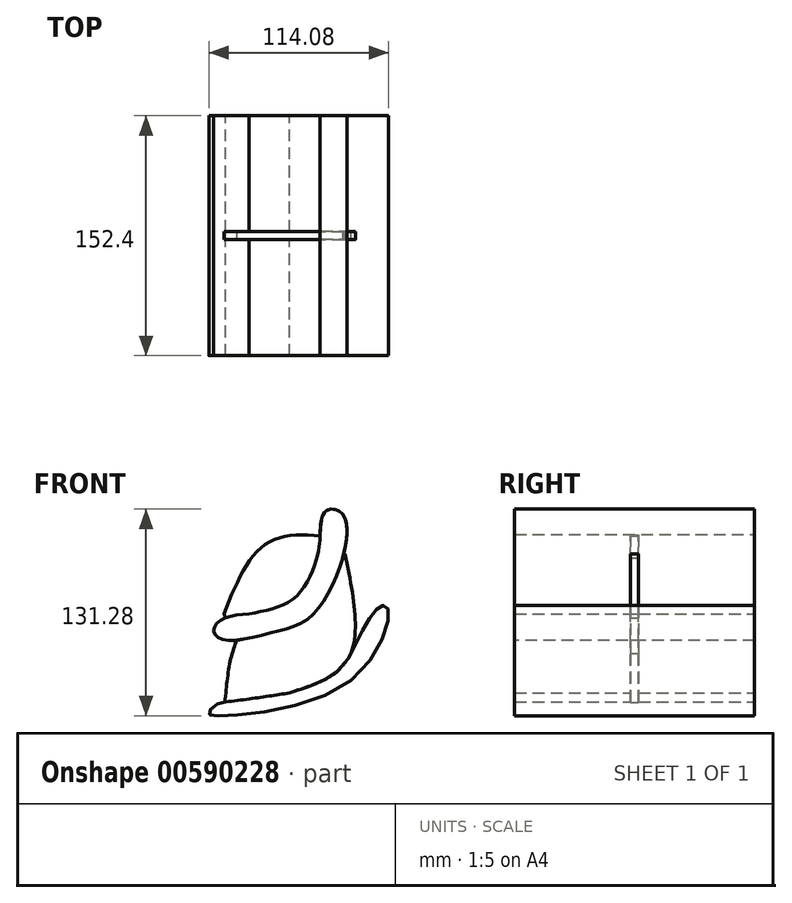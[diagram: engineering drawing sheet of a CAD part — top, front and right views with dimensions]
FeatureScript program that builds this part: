
annotation { "Feature Type Name" : "Feature", "Feature Type Description" : "" }
export const myFeature = defineFeature(function(context is Context, id is Id, definition is map)
    precondition{}
    {
        {
            var Q0;
            Q0=qCreatedBy(makeId("Front.planeOp"),FACE);
            var sketch = newSketch(context, id + "F0", { "sketchPlane" : qUnion([Q0])});
            skLineSegment(sketch, "E0.bottom", {"start": v(0, 0) * mm, "end": v(-60.89, 0) * mm});
            skFitSpline(sketch, "E1", {"points": [v(-60.89, 0) * mm, v(-30.65, 11.3) * mm, v(-16.9, 39.17) * mm, v(-15.76, 50.24) * mm], "startDerivative": vector(86.43, 14.9) * mm, "endDerivative": vector(0.82, 41.24) * mm});
            skFitSpline(sketch, "E2", {"points": [v(-60.89, 0) * mm, v(-77.99, -3.6) * mm, v(-83.33, -10.85) * mm, v(-77.22, -16.57) * mm, v(-44.77, -11.6) * mm, v(-16.9, 3.28) * mm, v(0, 60.93) * mm, v(-11.56, 65.51) * mm, v(-15.76, 50.24) * mm], "startDerivative": vector(-166.5, -14.14) * mm, "endDerivative": vector(-7.77, -179.5) * mm});
            skSolve(sketch);
        }
        {
            var Q0;
            Q0 = qSketchRegion(id + "F0", true);
            extrude(context, id + "F1", {"entities" : qUnion([Q0]), "depth" : 76.2 * mm, "offsetDistance" : 25.4 * mm, "hasSecondDirection" : true, "secondDirectionOppositeDirection" : true, "secondDirectionDepth" : 76.2 * mm});
        }
        {
            var Q0;
            Q0=qCreatedBy(makeId("Front.planeOp"),FACE);
            var sketch = newSketch(context, id + "F2", { "sketchPlane" : qUnion([Q0])});
            skFitSpline(sketch, "E3", {"points": [v(0, 47.17) * mm, v(-48.43, 45.32) * mm, v(-76.8, 0) * mm], "startDerivative": vector(-110, 16.86) * mm, "endDerivative": vector(-44.12, -110.16) * mm});
            skFitSpline(sketch, "E4", {"points": [v(-76.8, 0) * mm, v(-69.4, -10.17) * mm, v(-35.48, 0) * mm], "startDerivative": vector(13.4, -35.36) * mm, "endDerivative": vector(64.88, 29.86) * mm});
            skFitSpline(sketch, "E5", {"points": [v(-35.48, 0) * mm, v(0, 47.17) * mm], "startDerivative": vector(35.48, 47.17) * mm, "endDerivative": vector(35.48, 47.17) * mm});
            skSolve(sketch);
        }
        {
            var Q0;
            Q0 = qSketchRegion(id + "F2", true);
            extrude(context, id + "F3", {"entities" : qUnion([Q0]), "operationType" : NewBodyOperationType.ADD, "depth" : 2.54 * mm, "offsetDistance" : 25.4 * mm, "hasSecondDirection" : true, "secondDirectionOppositeDirection" : true, "secondDirectionDepth" : 2.54 * mm});
        }
        {
            var Q0;
            Q0=qCreatedBy(makeId("Front.planeOp"),FACE);
            var sketch = newSketch(context, id + "F4", { "sketchPlane" : qUnion([Q0])});
            skFitSpline(sketch, "E6", {"points": [v(0, 37.92) * mm, v(0, -32.68) * mm, v(-76.18, -56.42) * mm], "startDerivative": vector(35.83, -169.8) * mm, "endDerivative": vector(-185.92, -20.42) * mm});
            skFitSpline(sketch, "E7", {"points": [v(-76.18, -56.42) * mm, v(-68.78, -17.57) * mm, v(-53.98, 0) * mm], "startDerivative": vector(7.03, 76.36) * mm, "endDerivative": vector(38.8, 34.61) * mm});
            skFitSpline(sketch, "E8", {"points": [v(-53.98, 0) * mm, v(-20.99, 9.56) * mm, v(0, 37.92) * mm], "startDerivative": vector(72.57, 10.03) * mm, "endDerivative": vector(35.47, 65.7) * mm});
            skSolve(sketch);
        }
        {
            var Q0;
            Q0 = qSketchRegion(id + "F4", true);
            extrude(context, id + "F5", {"entities" : qUnion([Q0]), "operationType" : NewBodyOperationType.ADD, "depth" : 2.54 * mm, "offsetDistance" : 25.4 * mm, "hasSecondDirection" : true, "secondDirectionOppositeDirection" : true, "secondDirectionDepth" : 2.54 * mm});
        }
        {
            var Q0;
            Q0=qCreatedBy(makeId("Front.planeOp"),FACE);
            var sketch = newSketch(context, id + "F6", { "sketchPlane" : qUnion([Q0])});
            skFitSpline(sketch, "E9", {"points": [v(-75.7, -56.07) * mm, v(-83.02, -58.41) * mm, v(-86.3, -63.58) * mm, v(-79.96, -64.8) * mm, v(0, -45.12) * mm, v(27.75, 0) * mm, v(25.14, 5.35) * mm, v(19.97, 2.71) * mm, v(10.05, -13.09) * mm, v(-4.45, -36.35) * mm, v(-35.1, -50.27) * mm], "startDerivative": vector(-117.73, -40) * mm, "endDerivative": vector(-275.73, -94.64) * mm});
            skFitSpline(sketch, "E10", {"points": [v(-35.1, -50.27) * mm, v(-53.26, -53.1) * mm, v(-75.7, -56.07) * mm], "startDerivative": vector(-37.3, -6.07) * mm, "endDerivative": vector(-43.83, -5.54) * mm});
            skSolve(sketch);
        }
        {
            var Q0;
            Q0 = qSketchRegion(id + "F6", true);
            extrude(context, id + "F7", {"entities" : qUnion([Q0]), "operationType" : NewBodyOperationType.ADD, "depth" : 76.2 * mm, "offsetDistance" : 25.4 * mm, "hasSecondDirection" : true, "secondDirectionOppositeDirection" : true, "secondDirectionDepth" : 76.2 * mm});
        }
    });
